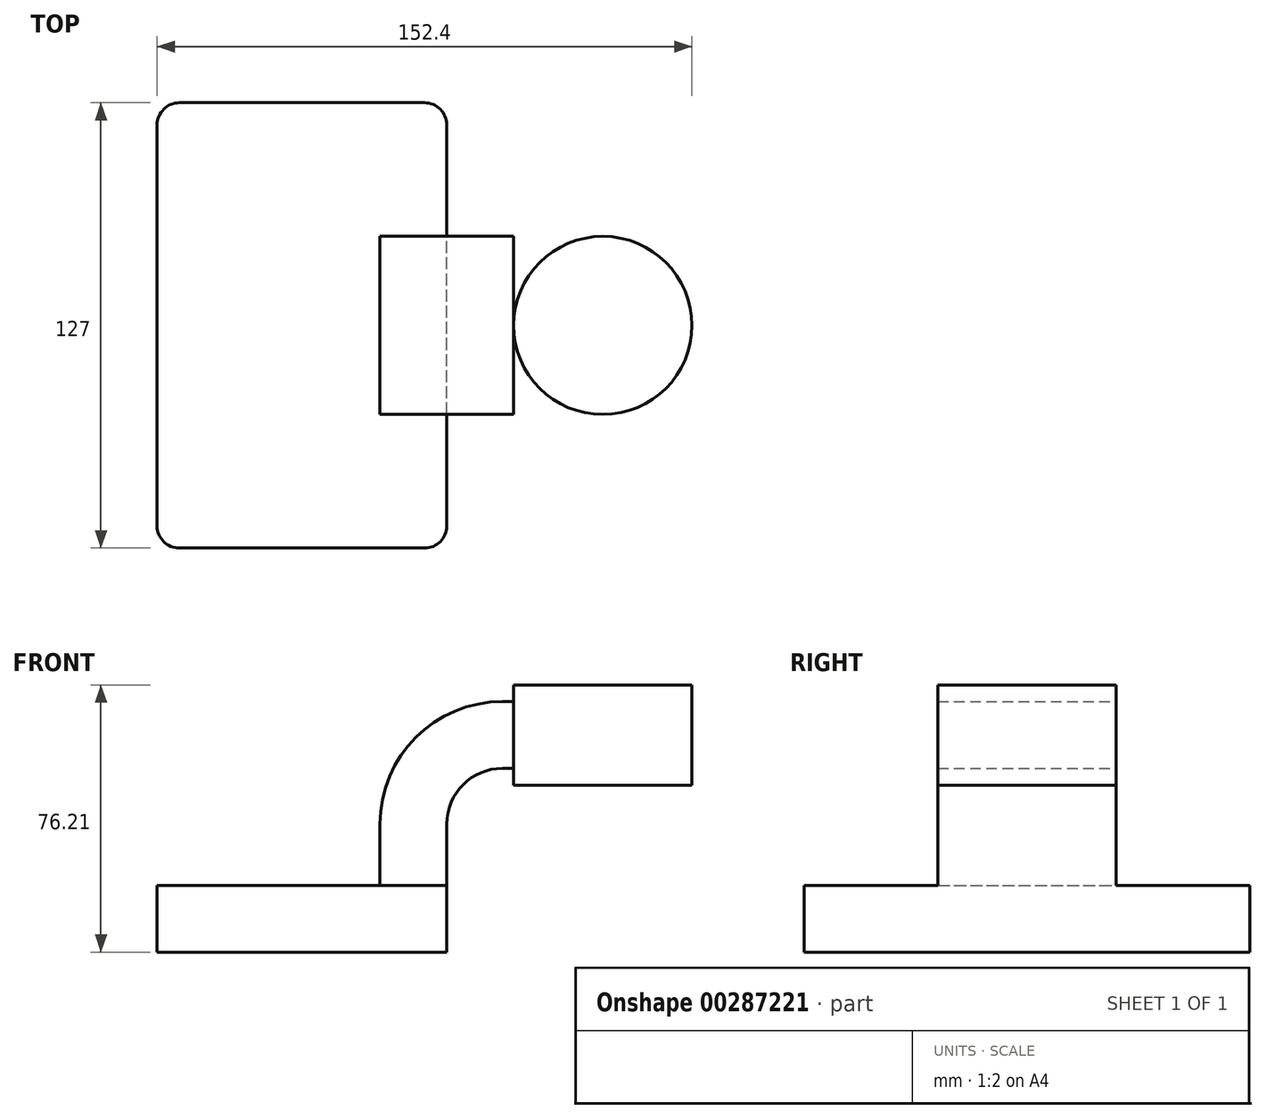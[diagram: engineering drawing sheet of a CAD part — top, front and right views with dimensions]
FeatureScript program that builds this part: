
annotation { "Feature Type Name" : "Feature", "Feature Type Description" : "" }
export const myFeature = defineFeature(function(context is Context, id is Id, definition is map)
    precondition{}
    {
        {
            var Q0;
            Q0=qCreatedBy(makeId("Front.planeOp"),FACE);
            var sketch = newSketch(context, id + "F0", { "sketchPlane" : qUnion([Q0])});
            skLineSegment(sketch, "E0.bottom", {"start": v(41.27, 9.53) * mm, "end": v(-41.28, 9.53) * mm});
            skLineSegment(sketch, "E0.top", {"start": v(41.28, -9.52) * mm, "end": v(-41.27, -9.52) * mm});
            skLineSegment(sketch, "E0.left", {"start": v(41.28, 9.53) * mm, "end": v(41.28, -9.52) * mm});
            skLineSegment(sketch, "E0.right", {"start": v(-41.28, 9.53) * mm, "end": v(-41.28, -9.52) * mm});
            skPoint(sketch, "E0.middle", {"position": v(0, 0) * mm});
            skLineSegment(sketch, "E1.bottom", {"start": v(60.32, 38.1) * mm, "end": v(111.12, 38.1) * mm});
            skLineSegment(sketch, "E1.top", {"start": v(60.32, 66.68) * mm, "end": v(111.12, 66.68) * mm});
            skLineSegment(sketch, "E1.left", {"start": v(60.32, 38.1) * mm, "end": v(60.32, 66.67) * mm});
            skLineSegment(sketch, "E1.right", {"start": v(111.13, 38.1) * mm, "end": v(111.13, 66.68) * mm});
            skPoint(sketch, "E1.middle", {"position": v(85.72, 52.39) * mm});
            skLineSegment(sketch, "E2", {"start": v(41.27, 9.53) * mm, "end": v(41.27, 27) * mm});
            skArc(sketch, "E3", {"start": v(41.27, 27) * mm, "mid": v(45.92, 38.23) * mm, "end": v(57.15, 42.88) * mm});
            skLineSegment(sketch, "E4", {"start": v(57.15, 42.88) * mm, "end": v(85.73, 42.88) * mm});
            skLineSegment(sketch, "E5.0", {"start": v(57.15, 61.93) * mm, "end": v(85.72, 61.93) * mm});
            skArc(sketch, "E5.1", {"start": v(22.23, 27) * mm, "mid": v(32.45, 51.7) * mm, "end": v(57.15, 61.93) * mm});
            skLineSegment(sketch, "E5.2", {"start": v(22.22, 9.53) * mm, "end": v(22.22, 27) * mm});
            skPoint(sketch, "E6", {"position": v(85.73, 38.1) * mm});
            skLineSegment(sketch, "E7", {"start": v(85.73, 38.1) * mm, "end": v(85.73, 66.68) * mm});
            skFitSpline(sketch, "E8", {"points": [v(-41.28, 9.53) * mm, v(57.15, 61.93) * mm], "startDerivative": vector(0, 99.35) * mm, "endDerivative": vector(182.38, -0.83) * mm});
            skSolve(sketch);
        }
        {
            var Q0;
            Q0=makeQuery(id+"F0.imprint","IMPRINT",FACE,{"disambiguationData":[TD([[makeQuery(id+"F0.imprint","IMPRINT",EDGE,{"derivedFrom":sQuery(id+"F0.wireOp",EDGE,"E0.top")}),-1.0]])]});
            extrude(context, id + "F1", {"entities" : qUnion([Q0]), "endBound" : BoundingType.SYMMETRIC, "depth" : 127 * mm});
        }
        {
            var Q0;
            {var subQ1=sQuery(id+"F0.wireOp",EDGE,"E2");Q0=makeQuery(id+"F0.imprint","IMPRINT",FACE,{"disambiguationData":[TD([[makeQuery(id+"F0.imprint","IMPRINT",EDGE,{"derivedFrom":subQ1}),1.0]])]});}
            extrude(context, id + "F2", {"entities" : qUnion([Q0]), "operationType" : NewBodyOperationType.ADD, "endBound" : BoundingType.SYMMETRIC, "depth" : 50.8 * mm});
        }
        {
            var Q0;
            Q0=makeQuery(id+"F0.imprint","IMPRINT",FACE,{"disambiguationData":[TD([[makeQuery(id+"F0.imprint","IMPRINT",EDGE,{"derivedFrom":sQuery(id+"F0.wireOp",EDGE,"E5.1")}),1.0]])]});
            extrude(context, id + "F3", {"entities" : qUnion([Q0]), "operationType" : NewBodyOperationType.ADD, "endBound" : BoundingType.SYMMETRIC, "depth" : 15.88 * mm});
        }
        {
            var Q0;
            {var subQ0=sQuery(id+"F0.wireOp",EDGE,"E1.right");Q0=makeQuery(id+"F0.imprint","IMPRINT",FACE,{"disambiguationData":[TD([[makeQuery(id+"F0.imprint","IMPRINT",EDGE,{"derivedFrom":subQ0}),1.0]])]});}
            var Q1;
            Q1=sQuery(id+"F0.wireOp",EDGE,"E7");
            revolve(context, id + "F4", {"operationType" : NewBodyOperationType.ADD, "entities" : qUnion([Q0]), "axis" : qUnion([Q1]), "revolveType" : RevolveType.FULL});
        }
        {
            var Q0;
            Q0=makeQuery(id+"F1.opExtrude","CAP_EDGE",EDGE,{"disambiguationData":[OSD([sQuery(id+"F0.wireOp",EDGE,"E0.left")])],"isStart":false});
            var Q1;
            Q1=makeQuery(id+"F1.opExtrude","CAP_EDGE",EDGE,{"disambiguationData":[OSD([sQuery(id+"F0.wireOp",EDGE,"E0.left")])],"isStart":true});
            var Q2;
            Q2=makeQuery(id+"F1.opExtrude","CAP_EDGE",EDGE,{"disambiguationData":[OSD([sQuery(id+"F0.wireOp",EDGE,"E0.right")])],"isStart":true});
            var Q3;
            Q3=makeQuery(id+"F1.opExtrude","CAP_EDGE",EDGE,{"disambiguationData":[OSD([sQuery(id+"F0.wireOp",EDGE,"E0.right")])],"isStart":false});
            fillet(context, id + "F5", {"entities" : qUnion([Q0, Q1, Q2, Q3]), "radius" : 6.35 * mm, "tangentPropagation" : true, "allowEdgeOverflow" : false});
        }
    });
